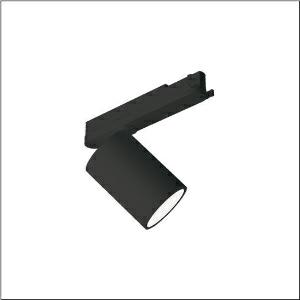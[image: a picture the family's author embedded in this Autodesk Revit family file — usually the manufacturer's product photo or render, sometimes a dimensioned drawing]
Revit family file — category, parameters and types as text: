
# Revit family: spot_31_51sf33mab4b
name_source: partatom
category: Lighting Fixtures
units: mm (PartAtom-declared; Revit-internal decimal feet)

## family parameters
Cut with Voids When Loaded = No
Host = Face
Light Source = No
Part Type = Normal
Room Calculation Point = No
Round Connector Dimension = Use Diameter
Shared = No

## types (1)
- --- (1 x LED, 5030 lm, 41.7 W, 3000K)
    Apparent Load = 42 VA
    CIE Flux Codes = 92 97 99 100 100
    Color Rendering = 90
    Color Temperature = 3000K
    Default Elevation = 1800 mm
    Description = Spot 31, directional spotlight, light control with lens, of PMMA, LED rated luminous flux: 4.830lm, light colour: 930, control gear: ECG Multilumen, with 3-phase adapter, mains connection: 220..240V, AC, 50/60Hz, of aluminium, jet black (RAL 9005), length: 213mm, diameter: 90mm, protection rating (complete): IP20, insulation class (complete): insulation class I (protective earthing), certification: CE, impact resistance: IK02, permissible ambient temperature for indoor applications: -20..+40°C, packaging unit: 1 piece
    Height = 175 mm
    Lamp = 1 x LED
    Lamp Light Flux = 5030 lm
    Lamp Power = 41.7 W
    Lamp count = 1
    Length = 90 mm
    Luminous efficacy = 121 lm/W
    Manufacturer = Siteco
    ModVariant = No
    Model = 51SF33MAB4B
    Mounting Place = Ceiling
    Mounting Type = Pendant
    Number of Poles = 1
    OnlyDefault = Yes
    Power Factor = 1
    Product Name = Spot 31
    Product group = directional spotlight
    ProductGroupID = 905
    Protection Class = Protection class I
    Protection Degree = IP 20
    RLX_Detail_Level = 1
    RLX_Emergency_Light_Flux = 0 lm
    RLX_Emergency_Type = 0
    RLX_Emergency_Type_DB = No
    RlxData = <blob elided: 20877 chars, md5=6ce5f54b>
    Socket = socket
    Standby Power = 0 W
    System Light Flux = 5030 lm
    System Power = 42 W
    Type Comments = factory setting: luminous flux: 100 % | (ON | ON | ON | ON) | 1050 mA
    Type Image = l_1273723.jpg
    URL = http://relux.com
    VarID = @adj_096051
    Voltage = 0 V
    Weight = 0.00 kg
    Width = 0 mm  [stored 0 ft]

note: [stored X ft] marks values corroborated as IEEE doubles in the binary element streams (Revit-internal decimal feet)

## geometry (parser evidence)
native form markers: Blend x4, Sweep x11
no freeform markers — native parametric forms only
